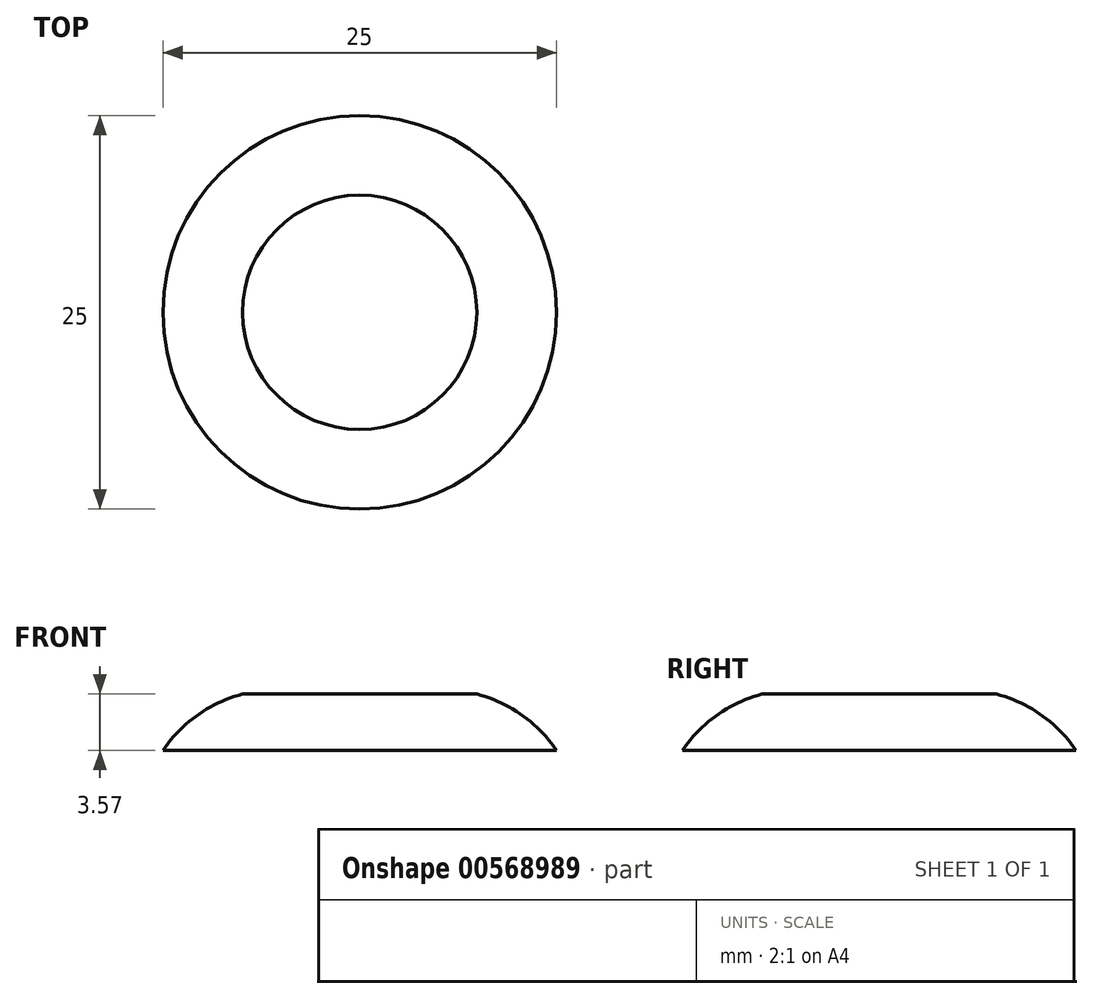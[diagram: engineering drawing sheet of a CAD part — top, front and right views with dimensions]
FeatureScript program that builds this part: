
annotation { "Feature Type Name" : "Feature", "Feature Type Description" : "" }
export const myFeature = defineFeature(function(context is Context, id is Id, definition is map)
    precondition{}
    {
        {
            var Q0;
            Q0=qCreatedBy(makeId("Front.planeOp"),FACE);
            var sketch = newSketch(context, id + "F0", { "sketchPlane" : qUnion([Q0])});
            skLineSegment(sketch, "E0", {"start": v(-12.5, -32.24) * mm, "end": v(12.5, -32.24) * mm});
            skLineSegment(sketch, "E1", {"start": v(-7.44, -28.67) * mm, "end": v(7.44, -28.67) * mm});
            skArc(sketch, "E2", {"start": v(-7.44, -28.67) * mm, "mid": v(-10.3, -30) * mm, "end": v(-12.5, -32.24) * mm});
            skArc(sketch, "E3", {"start": v(12.5, -32.24) * mm, "mid": v(10.3, -30) * mm, "end": v(7.44, -28.67) * mm});
            skLineSegment(sketch, "E4", {"start": v(0, -28.67) * mm, "end": v(0, -32.24) * mm});
            skSolve(sketch);
        }
        {
            var Q0;
            {var subQ0=sQuery(id+"F0.wireOp",EDGE,"E2");Q0=makeQuery(id+"F0.imprint","IMPRINT",FACE,{"disambiguationData":[TD([[makeQuery(id+"F0.imprint","IMPRINT",EDGE,{"derivedFrom":subQ0}),1.0]])]});}
            var Q1;
            Q1=sQuery(id+"F0.wireOp",EDGE,"E4");
            revolve(context, id + "F1", {"entities" : qUnion([Q0]), "axis" : qUnion([Q1]), "revolveType" : RevolveType.FULL});
        }
    });
